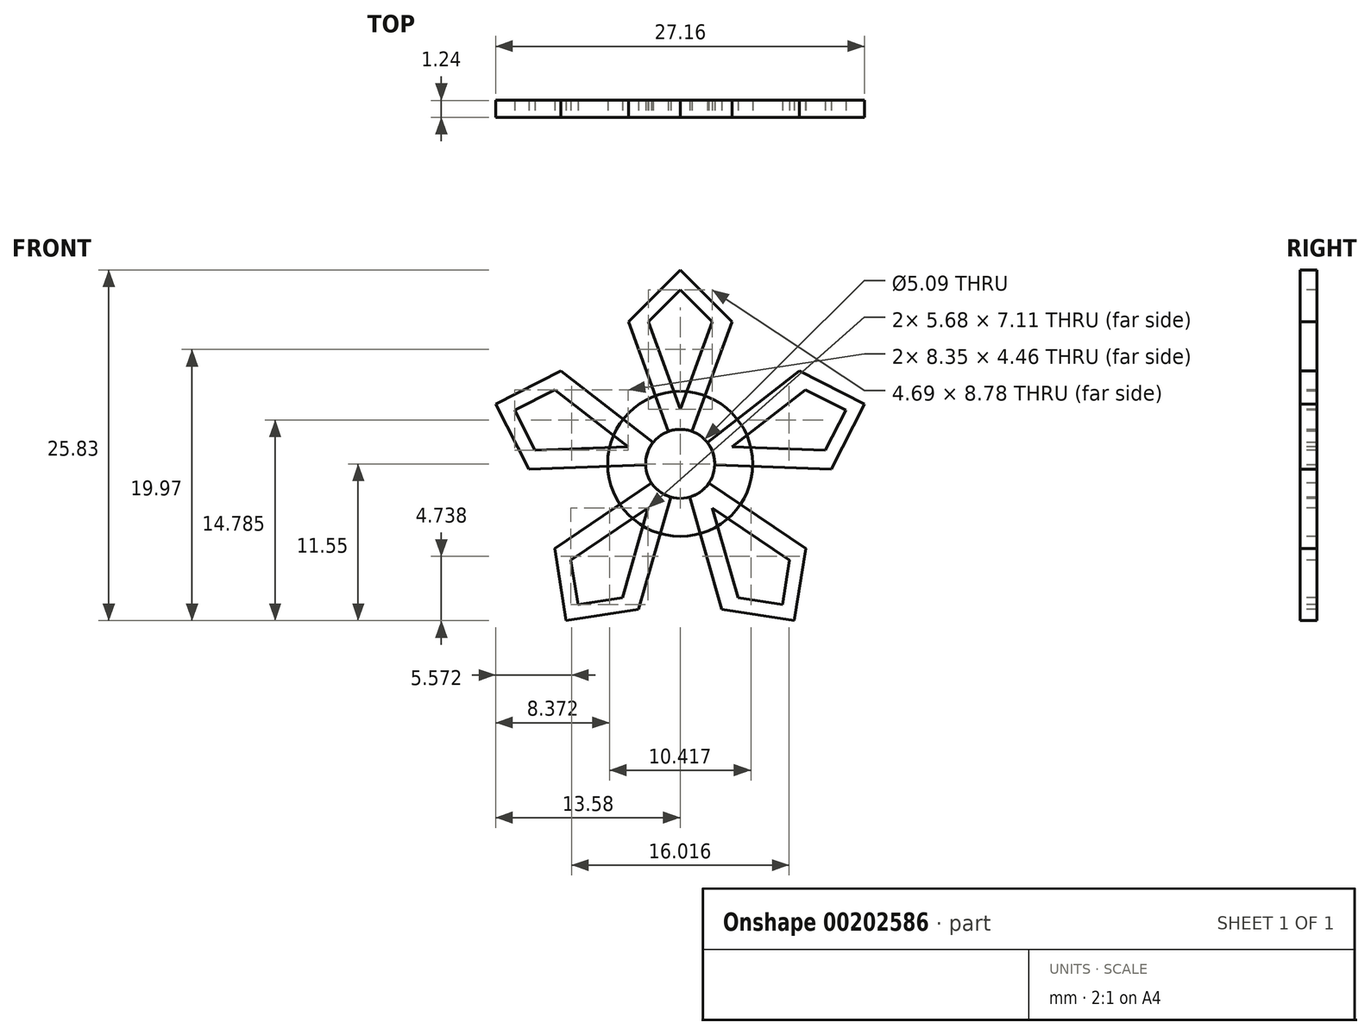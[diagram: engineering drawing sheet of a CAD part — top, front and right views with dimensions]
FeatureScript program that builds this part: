
annotation { "Feature Type Name" : "Feature", "Feature Type Description" : "" }
export const myFeature = defineFeature(function(context is Context, id is Id, definition is map)
    precondition{}
    {
        {
            var Q0;
            Q0=qCreatedBy(makeId("Front.planeOp"),FACE);
            var sketch = newSketch(context, id + "F0", { "sketchPlane" : qUnion([Q0])});
            skLineSegment(sketch, "E0", {"start": v(0, 0) * mm, "end": v(-3.8, 10.47) * mm});
            skLineSegment(sketch, "E1", {"start": v(-3.81, 10.47) * mm, "end": v(0, 14.28) * mm});
            skLineSegment(sketch, "E2", {"start": v(0, 14.28) * mm, "end": v(3.81, 10.47) * mm});
            skLineSegment(sketch, "E3", {"start": v(3.81, 10.47) * mm, "end": v(0, 0) * mm});
            skLineSegment(sketch, "E4", {"start": v(0, 4.03) * mm, "end": v(-2.34, 10.47) * mm});
            skLineSegment(sketch, "E5", {"start": v(-2.34, 10.47) * mm, "end": v(0, 12.81) * mm});
            skLineSegment(sketch, "E6", {"start": v(0, 12.81) * mm, "end": v(2.34, 10.47) * mm});
            skLineSegment(sketch, "E7", {"start": v(2.34, 10.47) * mm, "end": v(0, 4.03) * mm});
            skLineSegment(sketch, "E8.1.0", {"start": v(0, 0) * mm, "end": v(-11.13, -0.39) * mm});
            skLineSegment(sketch, "E8.1.1", {"start": v(-11.13, -0.39) * mm, "end": v(-13.58, 4.41) * mm});
            skLineSegment(sketch, "E8.1.2", {"start": v(-13.58, 4.41) * mm, "end": v(-8.78, 6.86) * mm});
            skLineSegment(sketch, "E8.1.3", {"start": v(-8.78, 6.86) * mm, "end": v(0, 0) * mm});
            skLineSegment(sketch, "E8.1.4", {"start": v(-3.83, 1.24) * mm, "end": v(-10.68, 1) * mm});
            skLineSegment(sketch, "E8.1.5", {"start": v(-10.68, 1) * mm, "end": v(-12.18, 3.96) * mm});
            skLineSegment(sketch, "E8.1.6", {"start": v(-12.18, 3.96) * mm, "end": v(-9.23, 5.46) * mm});
            skLineSegment(sketch, "E8.1.7", {"start": v(-9.23, 5.46) * mm, "end": v(-3.83, 1.24) * mm});
            skLineSegment(sketch, "E8.2.0", {"start": v(0, 0) * mm, "end": v(-3.07, -10.7) * mm});
            skLineSegment(sketch, "E8.2.1", {"start": v(-3.07, -10.7) * mm, "end": v(-8.4, -11.55) * mm});
            skLineSegment(sketch, "E8.2.2", {"start": v(-8.4, -11.55) * mm, "end": v(-9.24, -6.23) * mm});
            skLineSegment(sketch, "E8.2.3", {"start": v(-9.24, -6.23) * mm, "end": v(0, 0) * mm});
            skLineSegment(sketch, "E8.2.4", {"start": v(-2.37, -3.26) * mm, "end": v(-4.26, -9.85) * mm});
            skLineSegment(sketch, "E8.2.5", {"start": v(-4.26, -9.85) * mm, "end": v(-7.53, -10.36) * mm});
            skLineSegment(sketch, "E8.2.6", {"start": v(-7.53, -10.36) * mm, "end": v(-8.05, -7.1) * mm});
            skLineSegment(sketch, "E8.2.7", {"start": v(-8.05, -7.1) * mm, "end": v(-2.37, -3.26) * mm});
            skLineSegment(sketch, "E8.3.0", {"start": v(0, 0) * mm, "end": v(9.24, -6.23) * mm});
            skLineSegment(sketch, "E8.3.1", {"start": v(9.24, -6.23) * mm, "end": v(8.4, -11.55) * mm});
            skLineSegment(sketch, "E8.3.2", {"start": v(8.4, -11.55) * mm, "end": v(3.07, -10.7) * mm});
            skLineSegment(sketch, "E8.3.3", {"start": v(3.07, -10.7) * mm, "end": v(0, 0) * mm});
            skLineSegment(sketch, "E8.3.4", {"start": v(2.37, -3.26) * mm, "end": v(8.05, -7.1) * mm});
            skLineSegment(sketch, "E8.3.5", {"start": v(8.05, -7.1) * mm, "end": v(7.53, -10.36) * mm});
            skLineSegment(sketch, "E8.3.6", {"start": v(7.53, -10.36) * mm, "end": v(4.26, -9.85) * mm});
            skLineSegment(sketch, "E8.3.7", {"start": v(4.26, -9.85) * mm, "end": v(2.37, -3.26) * mm});
            skLineSegment(sketch, "E8.4.0", {"start": v(0, 0) * mm, "end": v(8.78, 6.86) * mm});
            skLineSegment(sketch, "E8.4.1", {"start": v(8.78, 6.86) * mm, "end": v(13.58, 4.41) * mm});
            skLineSegment(sketch, "E8.4.2", {"start": v(13.58, 4.41) * mm, "end": v(11.13, -0.39) * mm});
            skLineSegment(sketch, "E8.4.3", {"start": v(11.13, -0.39) * mm, "end": v(0, 0) * mm});
            skLineSegment(sketch, "E8.4.4", {"start": v(3.83, 1.24) * mm, "end": v(9.23, 5.46) * mm});
            skLineSegment(sketch, "E8.4.5", {"start": v(9.23, 5.46) * mm, "end": v(12.18, 3.96) * mm});
            skLineSegment(sketch, "E8.4.6", {"start": v(12.18, 3.96) * mm, "end": v(10.68, 1) * mm});
            skLineSegment(sketch, "E8.4.7", {"start": v(10.68, 1) * mm, "end": v(3.83, 1.24) * mm});
            skPoint(sketch, "E8.center", {"position": v(0, 0) * mm});
            skSolve(sketch);
        }
        {
            var Q0;
            Q0=makeQuery(id+"F0.imprint","IMPRINT",FACE,{"disambiguationData":[TD([[makeQuery(id+"F0.imprint","IMPRINT",EDGE,{"derivedFrom":sQuery(id+"F0.wireOp",EDGE,"E0")}),-1.0]])]});
            var Q1;
            Q1=makeQuery(id+"F0.imprint","IMPRINT",FACE,{"disambiguationData":[TD([[makeQuery(id+"F0.imprint","IMPRINT",EDGE,{"derivedFrom":sQuery(id+"F0.wireOp",EDGE,"E8.1.0")}),-1.0]])]});
            var Q2;
            Q2=makeQuery(id+"F0.imprint","IMPRINT",FACE,{"disambiguationData":[TD([[makeQuery(id+"F0.imprint","IMPRINT",EDGE,{"derivedFrom":sQuery(id+"F0.wireOp",EDGE,"E8.2.0")}),-1.0]])]});
            var Q3;
            Q3=makeQuery(id+"F0.imprint","IMPRINT",FACE,{"disambiguationData":[TD([[makeQuery(id+"F0.imprint","IMPRINT",EDGE,{"derivedFrom":sQuery(id+"F0.wireOp",EDGE,"E8.3.0")}),-1.0]])]});
            var Q4;
            Q4=makeQuery(id+"F0.imprint","IMPRINT",FACE,{"disambiguationData":[TD([[makeQuery(id+"F0.imprint","IMPRINT",EDGE,{"derivedFrom":sQuery(id+"F0.wireOp",EDGE,"E8.4.0")}),-1.0]])]});
            extrude(context, id + "F1", {"entities" : qUnion([Q0, Q1, Q2, Q3, Q4]), "oppositeDirection" : true, "depth" : 1.24 * mm});
        }
        {
            var Q0;
            Q0=qCreatedBy(makeId("Front.planeOp"),FACE);
            var sketch = newSketch(context, id + "F2", { "sketchPlane" : qUnion([Q0])});
            skCircle(sketch, "E9", {"center": v(0, 0) * mm, "radius": 5.34 * mm});
            skSolve(sketch);
        }
        {
            var Q0;
            Q0=makeQuery(id+"F2.imprint","IMPRINT",FACE,{"disambiguationData":[TD([[makeQuery(id+"F2.imprint","IMPRINT",EDGE,{"derivedFrom":sQuery(id+"F2.wireOp",EDGE,"E9")}),1.0]])]});
            extrude(context, id + "F3", {"entities" : qUnion([Q0]), "oppositeDirection" : true, "depth" : 1.24 * mm});
        }
        {
            var Q0;
            Q0=qCreatedBy(makeId("Front.planeOp"),FACE);
            var sketch = newSketch(context, id + "F4", { "sketchPlane" : qUnion([Q0])});
            skCircle(sketch, "E10", {"center": v(0, 0) * mm, "radius": 2.54 * mm});
            skSolve(sketch);
        }
        {
            var Q0;
            Q0=makeQuery(id+"F4.imprint","IMPRINT",FACE,{"disambiguationData":[TD([[makeQuery(id+"F4.imprint","IMPRINT",EDGE,{"derivedFrom":sQuery(id+"F4.wireOp",EDGE,"E10")}),1.0]])]});
            extrude(context, id + "F5", {"entities" : qUnion([Q0]), "operationType" : NewBodyOperationType.REMOVE, "oppositeDirection" : true, "depth" : 1.27 * mm});
        }
    });
